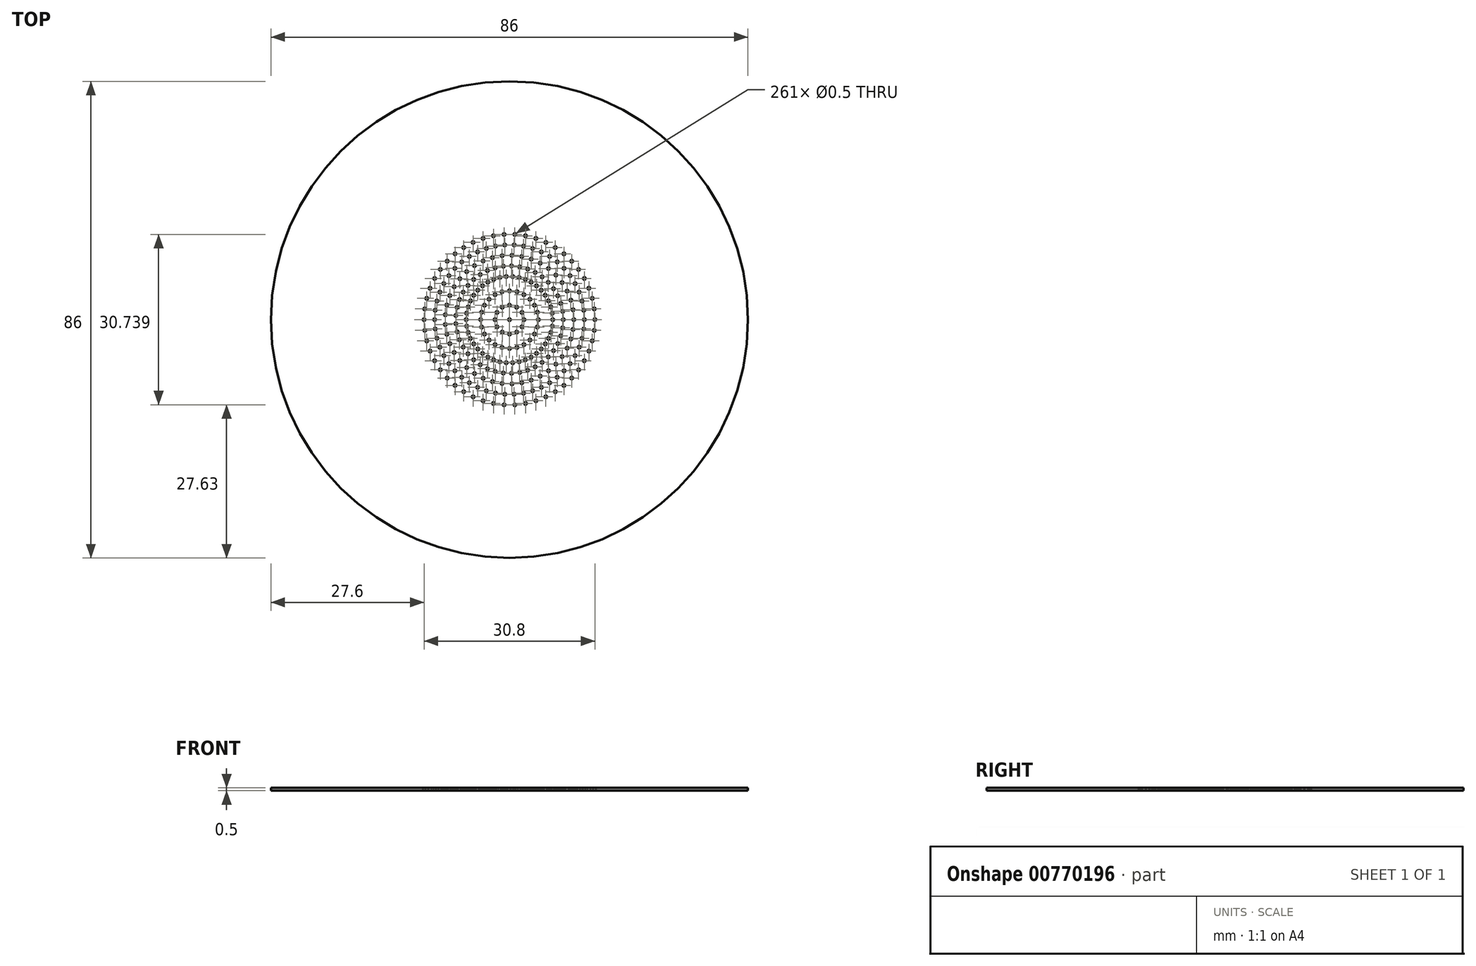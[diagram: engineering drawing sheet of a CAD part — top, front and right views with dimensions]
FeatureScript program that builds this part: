
annotation { "Feature Type Name" : "Feature", "Feature Type Description" : "" }
export const myFeature = defineFeature(function(context is Context, id is Id, definition is map)
    precondition{}
    {
        {
            var Q0;
            Q0=qCreatedBy(makeId("Top.planeOp"),FACE);
            var sketch = newSketch(context, id + "F0", { "sketchPlane" : qUnion([Q0])});
            skCircle(sketch, "E0", {"center": v(0, 0) * mm, "radius": 43 * mm});
            skCircle(sketch, "E1", {"center": v(0, 0) * mm, "radius": 16.13 * mm, "construction": true});
            skCircle(sketch, "E2", {"center": v(0, 0) * mm, "radius": 12.7 * mm, "construction": true});
            skCircle(sketch, "E3", {"center": v(0, 0) * mm, "radius": 8.9 * mm, "construction": true});
            skSolve(sketch);
        }
        {
            var Q0;
            Q0=makeQuery(id+"F0.imprint","IMPRINT",FACE,{"disambiguationData":[TD([[makeQuery(id+"F0.imprint","IMPRINT",EDGE,{"derivedFrom":sQuery(id+"F0.wireOp",EDGE,"E0")}),1.0]])]});
            extrude(context, id + "F1", {"entities" : qUnion([Q0]), "oppositeDirection" : true, "depth" : 0.5 * mm, "offsetDistance" : 25 * mm});
        }
        {
            var Q0;
            Q0=makeQuery(id+"F0.imprint","IMPRINT",FACE,{"disambiguationData":[TD([[makeQuery(id+"F0.imprint","IMPRINT",EDGE,{"derivedFrom":sQuery(id+"F0.wireOp",EDGE,"E0")}),1.0]])]});
            var sketch = newSketch(context, id + "F2", { "sketchPlane" : qUnion([Q0])});
            skCircle(sketch, "E4", {"center": v(0, 0) * mm, "radius": 0.25 * mm});
            skSolve(sketch);
        }
        {
            var Q0;
            Q0=makeQuery(id+"F0.imprint","IMPRINT",FACE,{"disambiguationData":[TD([[makeQuery(id+"F0.imprint","IMPRINT",EDGE,{"derivedFrom":sQuery(id+"F0.wireOp",EDGE,"E0")}),1.0]])]});
            var sketch = newSketch(context, id + "F3", { "sketchPlane" : qUnion([Q0])});
            skCircle(sketch, "E5.0", {"center": v(0, 0) * mm, "radius": 0.25 * mm});
            skCircle(sketch, "E6.1.0.0", {"center": v(2.6, 0) * mm, "radius": 0.25 * mm});
            skCircle(sketch, "E6.2.0.0", {"center": v(5.2, 0) * mm, "radius": 0.25 * mm});
            skCircle(sketch, "E6.3.0.0", {"center": v(7.8, 0) * mm, "radius": 0.25 * mm});
            skLineSegment(sketch, "E6.direction1", {"start": v(0, 0) * mm, "end": v(2.6, 0) * mm, "construction": true});
            skCircle(sketch, "E7.1.0", {"center": v(2.25, 1.3) * mm, "radius": 0.25 * mm});
            skCircle(sketch, "E7.2.0", {"center": v(1.3, 2.25) * mm, "radius": 0.25 * mm});
            skCircle(sketch, "E7.3.0", {"center": v(0, 2.6) * mm, "radius": 0.25 * mm});
            skCircle(sketch, "E7.4.0", {"center": v(-1.3, 2.25) * mm, "radius": 0.25 * mm});
            skCircle(sketch, "E7.5.0", {"center": v(-2.25, 1.3) * mm, "radius": 0.25 * mm});
            skCircle(sketch, "E7.6.0", {"center": v(-2.6, 0) * mm, "radius": 0.25 * mm});
            skCircle(sketch, "E7.7.0", {"center": v(-2.25, -1.3) * mm, "radius": 0.25 * mm});
            skCircle(sketch, "E7.8.0", {"center": v(-1.3, -2.25) * mm, "radius": 0.25 * mm});
            skCircle(sketch, "E7.9.0", {"center": v(0, -2.6) * mm, "radius": 0.25 * mm});
            skCircle(sketch, "E7.10.0", {"center": v(1.3, -2.25) * mm, "radius": 0.25 * mm});
            skCircle(sketch, "E7.11.0", {"center": v(2.25, -1.3) * mm, "radius": 0.25 * mm});
            skCircle(sketch, "E8.1.0", {"center": v(5.02, 1.35) * mm, "radius": 0.25 * mm});
            skCircle(sketch, "E8.2.0", {"center": v(4.5, 2.6) * mm, "radius": 0.25 * mm});
            skCircle(sketch, "E8.3.0", {"center": v(3.68, 3.68) * mm, "radius": 0.25 * mm});
            skCircle(sketch, "E8.4.0", {"center": v(2.6, 4.5) * mm, "radius": 0.25 * mm});
            skCircle(sketch, "E8.5.0", {"center": v(1.35, 5.02) * mm, "radius": 0.25 * mm});
            skCircle(sketch, "E8.6.0", {"center": v(0, 5.2) * mm, "radius": 0.25 * mm});
            skCircle(sketch, "E8.7.0", {"center": v(-1.35, 5.02) * mm, "radius": 0.25 * mm});
            skCircle(sketch, "E8.8.0", {"center": v(-2.6, 4.5) * mm, "radius": 0.25 * mm});
            skCircle(sketch, "E8.9.0", {"center": v(-3.68, 3.68) * mm, "radius": 0.25 * mm});
            skCircle(sketch, "E8.10.0", {"center": v(-4.5, 2.6) * mm, "radius": 0.25 * mm});
            skCircle(sketch, "E8.11.0", {"center": v(-5.02, 1.35) * mm, "radius": 0.25 * mm});
            skCircle(sketch, "E8.12.0", {"center": v(-5.2, 0) * mm, "radius": 0.25 * mm});
            skCircle(sketch, "E8.13.0", {"center": v(-5.02, -1.35) * mm, "radius": 0.25 * mm});
            skCircle(sketch, "E8.14.0", {"center": v(-4.5, -2.6) * mm, "radius": 0.25 * mm});
            skCircle(sketch, "E8.15.0", {"center": v(-3.68, -3.68) * mm, "radius": 0.25 * mm});
            skCircle(sketch, "E8.16.0", {"center": v(-2.6, -4.5) * mm, "radius": 0.25 * mm});
            skCircle(sketch, "E8.17.0", {"center": v(-1.35, -5.02) * mm, "radius": 0.25 * mm});
            skCircle(sketch, "E8.18.0", {"center": v(0, -5.2) * mm, "radius": 0.25 * mm});
            skCircle(sketch, "E8.19.0", {"center": v(1.35, -5.02) * mm, "radius": 0.25 * mm});
            skCircle(sketch, "E8.20.0", {"center": v(2.6, -4.5) * mm, "radius": 0.25 * mm});
            skCircle(sketch, "E8.21.0", {"center": v(3.68, -3.68) * mm, "radius": 0.25 * mm});
            skCircle(sketch, "E8.22.0", {"center": v(4.5, -2.6) * mm, "radius": 0.25 * mm});
            skCircle(sketch, "E8.23.0", {"center": v(5.02, -1.35) * mm, "radius": 0.25 * mm});
            skCircle(sketch, "E9.1.0", {"center": v(7.71, 1.16) * mm, "radius": 0.25 * mm});
            skCircle(sketch, "E9.2.0", {"center": v(7.45, 2.3) * mm, "radius": 0.25 * mm});
            skCircle(sketch, "E9.3.0", {"center": v(7.03, 3.38) * mm, "radius": 0.25 * mm});
            skCircle(sketch, "E9.4.0", {"center": v(6.44, 4.4) * mm, "radius": 0.25 * mm});
            skCircle(sketch, "E9.5.0", {"center": v(5.72, 5.3) * mm, "radius": 0.25 * mm});
            skCircle(sketch, "E9.6.0", {"center": v(4.86, 6.1) * mm, "radius": 0.25 * mm});
            skCircle(sketch, "E9.7.0", {"center": v(3.9, 6.75) * mm, "radius": 0.25 * mm});
            skCircle(sketch, "E9.8.0", {"center": v(2.85, 7.26) * mm, "radius": 0.25 * mm});
            skCircle(sketch, "E9.9.0", {"center": v(1.74, 7.6) * mm, "radius": 0.25 * mm});
            skCircle(sketch, "E9.10.0", {"center": v(0.58, 7.78) * mm, "radius": 0.25 * mm});
            skCircle(sketch, "E9.11.0", {"center": v(-0.58, 7.78) * mm, "radius": 0.25 * mm});
            skCircle(sketch, "E9.12.0", {"center": v(-1.74, 7.6) * mm, "radius": 0.25 * mm});
            skCircle(sketch, "E9.13.0", {"center": v(-2.85, 7.26) * mm, "radius": 0.25 * mm});
            skCircle(sketch, "E9.14.0", {"center": v(-3.9, 6.75) * mm, "radius": 0.25 * mm});
            skCircle(sketch, "E9.15.0", {"center": v(-4.86, 6.1) * mm, "radius": 0.25 * mm});
            skCircle(sketch, "E9.16.0", {"center": v(-5.72, 5.3) * mm, "radius": 0.25 * mm});
            skCircle(sketch, "E9.17.0", {"center": v(-6.44, 4.4) * mm, "radius": 0.25 * mm});
            skCircle(sketch, "E9.18.0", {"center": v(-7.03, 3.38) * mm, "radius": 0.25 * mm});
            skCircle(sketch, "E9.19.0", {"center": v(-7.45, 2.3) * mm, "radius": 0.25 * mm});
            skCircle(sketch, "E9.20.0", {"center": v(-7.71, 1.16) * mm, "radius": 0.25 * mm});
            skCircle(sketch, "E9.21.0", {"center": v(-7.8, 0) * mm, "radius": 0.25 * mm});
            skCircle(sketch, "E9.22.0", {"center": v(-7.71, -1.16) * mm, "radius": 0.25 * mm});
            skCircle(sketch, "E9.23.0", {"center": v(-7.45, -2.3) * mm, "radius": 0.25 * mm});
            skCircle(sketch, "E9.24.0", {"center": v(-7.03, -3.38) * mm, "radius": 0.25 * mm});
            skCircle(sketch, "E9.25.0", {"center": v(-6.44, -4.4) * mm, "radius": 0.25 * mm});
            skCircle(sketch, "E9.26.0", {"center": v(-5.72, -5.3) * mm, "radius": 0.25 * mm});
            skCircle(sketch, "E9.27.0", {"center": v(-4.86, -6.1) * mm, "radius": 0.25 * mm});
            skCircle(sketch, "E9.28.0", {"center": v(-3.9, -6.75) * mm, "radius": 0.25 * mm});
            skCircle(sketch, "E9.29.0", {"center": v(-2.85, -7.26) * mm, "radius": 0.25 * mm});
            skCircle(sketch, "E9.30.0", {"center": v(-1.74, -7.6) * mm, "radius": 0.25 * mm});
            skCircle(sketch, "E9.31.0", {"center": v(-0.58, -7.78) * mm, "radius": 0.25 * mm});
            skCircle(sketch, "E9.32.0", {"center": v(0.58, -7.78) * mm, "radius": 0.25 * mm});
            skCircle(sketch, "E9.33.0", {"center": v(1.74, -7.6) * mm, "radius": 0.25 * mm});
            skCircle(sketch, "E9.34.0", {"center": v(2.85, -7.26) * mm, "radius": 0.25 * mm});
            skCircle(sketch, "E9.35.0", {"center": v(3.9, -6.75) * mm, "radius": 0.25 * mm});
            skCircle(sketch, "E9.36.0", {"center": v(4.86, -6.1) * mm, "radius": 0.25 * mm});
            skCircle(sketch, "E9.37.0", {"center": v(5.72, -5.3) * mm, "radius": 0.25 * mm});
            skCircle(sketch, "E9.38.0", {"center": v(6.44, -4.4) * mm, "radius": 0.25 * mm});
            skCircle(sketch, "E9.39.0", {"center": v(7.03, -3.38) * mm, "radius": 0.25 * mm});
            skCircle(sketch, "E9.40.0", {"center": v(7.45, -2.3) * mm, "radius": 0.25 * mm});
            skCircle(sketch, "E9.41.0", {"center": v(7.71, -1.16) * mm, "radius": 0.25 * mm});
            skSolve(sketch);
        }
        {
            var Q0;
            Q0=makeQuery(id+"F0.imprint","IMPRINT",FACE,{"disambiguationData":[TD([[makeQuery(id+"F0.imprint","IMPRINT",EDGE,{"derivedFrom":sQuery(id+"F0.wireOp",EDGE,"E0")}),1.0]])]});
            var sketch = newSketch(context, id + "F4", { "sketchPlane" : qUnion([Q0])});
            skCircle(sketch, "E10.0", {"center": v(7.8, 0) * mm, "radius": 0.25 * mm});
            skCircle(sketch, "E11.1.0.0", {"center": v(9.7, 0) * mm, "radius": 0.25 * mm});
            skCircle(sketch, "E11.2.0.0", {"center": v(11.6, 0) * mm, "radius": 0.25 * mm});
            skLineSegment(sketch, "E11.direction1", {"start": v(7.8, 0) * mm, "end": v(9.7, 0) * mm, "construction": true});
            skCircle(sketch, "E12.1.0", {"center": v(9.59, 1.48) * mm, "radius": 0.25 * mm});
            skCircle(sketch, "E12.1.1", {"center": v(11.46, 1.77) * mm, "radius": 0.25 * mm});
            skCircle(sketch, "E12.2.0", {"center": v(9.25, 2.93) * mm, "radius": 0.25 * mm});
            skCircle(sketch, "E12.2.1", {"center": v(11.06, 3.5) * mm, "radius": 0.25 * mm});
            skCircle(sketch, "E12.3.0", {"center": v(8.7, 4.3) * mm, "radius": 0.25 * mm});
            skCircle(sketch, "E12.3.1", {"center": v(10.4, 5.15) * mm, "radius": 0.25 * mm});
            skCircle(sketch, "E12.4.0", {"center": v(7.93, 5.58) * mm, "radius": 0.25 * mm});
            skCircle(sketch, "E12.4.1", {"center": v(9.49, 6.67) * mm, "radius": 0.25 * mm});
            skCircle(sketch, "E12.5.0", {"center": v(6.99, 6.73) * mm, "radius": 0.25 * mm});
            skCircle(sketch, "E12.5.1", {"center": v(8.36, 8.04) * mm, "radius": 0.25 * mm});
            skCircle(sketch, "E12.6.0", {"center": v(5.88, 7.71) * mm, "radius": 0.25 * mm});
            skCircle(sketch, "E12.6.1", {"center": v(7.03, 9.23) * mm, "radius": 0.25 * mm});
            skCircle(sketch, "E12.7.0", {"center": v(4.63, 8.52) * mm, "radius": 0.25 * mm});
            skCircle(sketch, "E12.7.1", {"center": v(5.54, 10.2) * mm, "radius": 0.25 * mm});
            skCircle(sketch, "E12.8.0", {"center": v(3.28, 9.13) * mm, "radius": 0.25 * mm});
            skCircle(sketch, "E12.8.1", {"center": v(3.92, 10.92) * mm, "radius": 0.25 * mm});
            skCircle(sketch, "E12.9.0", {"center": v(1.85, 9.52) * mm, "radius": 0.25 * mm});
            skCircle(sketch, "E12.9.1", {"center": v(2.2, 11.39) * mm, "radius": 0.25 * mm});
            skCircle(sketch, "E12.10.0", {"center": v(0.37, 9.7) * mm, "radius": 0.25 * mm});
            skCircle(sketch, "E12.10.1", {"center": v(0.44, 11.6) * mm, "radius": 0.25 * mm});
            skCircle(sketch, "E12.11.0", {"center": v(-1.11, 9.64) * mm, "radius": 0.25 * mm});
            skCircle(sketch, "E12.11.1", {"center": v(-1.33, 11.52) * mm, "radius": 0.25 * mm});
            skCircle(sketch, "E12.12.0", {"center": v(-2.57, 9.35) * mm, "radius": 0.25 * mm});
            skCircle(sketch, "E12.12.1", {"center": v(-3.07, 11.19) * mm, "radius": 0.25 * mm});
            skCircle(sketch, "E12.13.0", {"center": v(-3.97, 8.85) * mm, "radius": 0.25 * mm});
            skCircle(sketch, "E12.13.1", {"center": v(-4.75, 10.59) * mm, "radius": 0.25 * mm});
            skCircle(sketch, "E12.14.0", {"center": v(-5.27, 8.14) * mm, "radius": 0.25 * mm});
            skCircle(sketch, "E12.14.1", {"center": v(-6.3, 9.74) * mm, "radius": 0.25 * mm});
            skCircle(sketch, "E12.15.0", {"center": v(-6.45, 7.24) * mm, "radius": 0.25 * mm});
            skCircle(sketch, "E12.15.1", {"center": v(-7.72, 8.66) * mm, "radius": 0.25 * mm});
            skCircle(sketch, "E12.16.0", {"center": v(-7.48, 6.17) * mm, "radius": 0.25 * mm});
            skCircle(sketch, "E12.16.1", {"center": v(-8.95, 7.38) * mm, "radius": 0.25 * mm});
            skCircle(sketch, "E12.17.0", {"center": v(-8.34, 4.96) * mm, "radius": 0.25 * mm});
            skCircle(sketch, "E12.17.1", {"center": v(-9.97, 5.93) * mm, "radius": 0.25 * mm});
            skCircle(sketch, "E12.18.0", {"center": v(-9, 3.63) * mm, "radius": 0.25 * mm});
            skCircle(sketch, "E12.18.1", {"center": v(-10.76, 4.34) * mm, "radius": 0.25 * mm});
            skCircle(sketch, "E12.19.0", {"center": v(-9.44, 2.21) * mm, "radius": 0.25 * mm});
            skCircle(sketch, "E12.19.1", {"center": v(-11.3, 2.64) * mm, "radius": 0.25 * mm});
            skCircle(sketch, "E12.20.0", {"center": v(-9.67, 0.74) * mm, "radius": 0.25 * mm});
            skCircle(sketch, "E12.20.1", {"center": v(-11.57, 0.89) * mm, "radius": 0.25 * mm});
            skCircle(sketch, "E12.21.0", {"center": v(-9.67, -0.74) * mm, "radius": 0.25 * mm});
            skCircle(sketch, "E12.21.1", {"center": v(-11.57, -0.89) * mm, "radius": 0.25 * mm});
            skCircle(sketch, "E12.22.0", {"center": v(-9.44, -2.21) * mm, "radius": 0.25 * mm});
            skCircle(sketch, "E12.22.1", {"center": v(-11.3, -2.64) * mm, "radius": 0.25 * mm});
            skCircle(sketch, "E12.23.0", {"center": v(-9, -3.63) * mm, "radius": 0.25 * mm});
            skCircle(sketch, "E12.23.1", {"center": v(-10.76, -4.34) * mm, "radius": 0.25 * mm});
            skCircle(sketch, "E12.24.0", {"center": v(-8.34, -4.96) * mm, "radius": 0.25 * mm});
            skCircle(sketch, "E12.24.1", {"center": v(-9.97, -5.93) * mm, "radius": 0.25 * mm});
            skCircle(sketch, "E12.25.0", {"center": v(-7.48, -6.17) * mm, "radius": 0.25 * mm});
            skCircle(sketch, "E12.25.1", {"center": v(-8.95, -7.38) * mm, "radius": 0.25 * mm});
            skCircle(sketch, "E12.26.0", {"center": v(-6.45, -7.24) * mm, "radius": 0.25 * mm});
            skCircle(sketch, "E12.26.1", {"center": v(-7.72, -8.66) * mm, "radius": 0.25 * mm});
            skCircle(sketch, "E12.27.0", {"center": v(-5.27, -8.14) * mm, "radius": 0.25 * mm});
            skCircle(sketch, "E12.27.1", {"center": v(-6.3, -9.74) * mm, "radius": 0.25 * mm});
            skCircle(sketch, "E12.28.0", {"center": v(-3.97, -8.85) * mm, "radius": 0.25 * mm});
            skCircle(sketch, "E12.28.1", {"center": v(-4.75, -10.59) * mm, "radius": 0.25 * mm});
            skCircle(sketch, "E12.29.0", {"center": v(-2.57, -9.35) * mm, "radius": 0.25 * mm});
            skCircle(sketch, "E12.29.1", {"center": v(-3.07, -11.19) * mm, "radius": 0.25 * mm});
            skCircle(sketch, "E12.30.0", {"center": v(-1.11, -9.64) * mm, "radius": 0.25 * mm});
            skCircle(sketch, "E12.30.1", {"center": v(-1.33, -11.52) * mm, "radius": 0.25 * mm});
            skCircle(sketch, "E12.31.0", {"center": v(0.37, -9.7) * mm, "radius": 0.25 * mm});
            skCircle(sketch, "E12.31.1", {"center": v(0.44, -11.6) * mm, "radius": 0.25 * mm});
            skCircle(sketch, "E12.32.0", {"center": v(1.85, -9.52) * mm, "radius": 0.25 * mm});
            skCircle(sketch, "E12.32.1", {"center": v(2.2, -11.39) * mm, "radius": 0.25 * mm});
            skCircle(sketch, "E12.33.0", {"center": v(3.28, -9.13) * mm, "radius": 0.25 * mm});
            skCircle(sketch, "E12.33.1", {"center": v(3.92, -10.92) * mm, "radius": 0.25 * mm});
            skCircle(sketch, "E12.34.0", {"center": v(4.63, -8.52) * mm, "radius": 0.25 * mm});
            skCircle(sketch, "E12.34.1", {"center": v(5.54, -10.2) * mm, "radius": 0.25 * mm});
            skCircle(sketch, "E12.35.0", {"center": v(5.88, -7.71) * mm, "radius": 0.25 * mm});
            skCircle(sketch, "E12.35.1", {"center": v(7.03, -9.23) * mm, "radius": 0.25 * mm});
            skCircle(sketch, "E12.36.0", {"center": v(6.99, -6.73) * mm, "radius": 0.25 * mm});
            skCircle(sketch, "E12.36.1", {"center": v(8.36, -8.04) * mm, "radius": 0.25 * mm});
            skCircle(sketch, "E12.37.0", {"center": v(7.93, -5.58) * mm, "radius": 0.25 * mm});
            skCircle(sketch, "E12.37.1", {"center": v(9.49, -6.67) * mm, "radius": 0.25 * mm});
            skCircle(sketch, "E12.38.0", {"center": v(8.7, -4.3) * mm, "radius": 0.25 * mm});
            skCircle(sketch, "E12.38.1", {"center": v(10.4, -5.15) * mm, "radius": 0.25 * mm});
            skCircle(sketch, "E12.39.0", {"center": v(9.25, -2.93) * mm, "radius": 0.25 * mm});
            skCircle(sketch, "E12.39.1", {"center": v(11.06, -3.5) * mm, "radius": 0.25 * mm});
            skCircle(sketch, "E12.40.0", {"center": v(9.59, -1.48) * mm, "radius": 0.25 * mm});
            skCircle(sketch, "E12.40.1", {"center": v(11.46, -1.77) * mm, "radius": 0.25 * mm});
            skPoint(sketch, "E12.center", {"position": v(0, 0) * mm});
            skSolve(sketch);
        }
        {
            var Q0;
            Q0=makeQuery(id+"F0.imprint","IMPRINT",FACE,{"disambiguationData":[TD([[makeQuery(id+"F0.imprint","IMPRINT",EDGE,{"derivedFrom":sQuery(id+"F0.wireOp",EDGE,"E0")}),1.0]])]});
            var sketch = newSketch(context, id + "F5", { "sketchPlane" : qUnion([Q0])});
            skCircle(sketch, "E13.0", {"center": v(11.6, 0) * mm, "radius": 0.25 * mm});
            skCircle(sketch, "E14.1.0.0", {"center": v(13.5, 0) * mm, "radius": 0.25 * mm});
            skCircle(sketch, "E14.2.0.0", {"center": v(15.4, 0) * mm, "radius": 0.25 * mm});
            skLineSegment(sketch, "E14.direction1", {"start": v(11.6, 0) * mm, "end": v(13.5, 0) * mm, "construction": true});
            skCircle(sketch, "E15.1.0", {"center": v(13.4, 1.7) * mm, "radius": 0.25 * mm});
            skCircle(sketch, "E15.1.1", {"center": v(15.28, 1.93) * mm, "radius": 0.25 * mm});
            skCircle(sketch, "E15.2.0", {"center": v(13.08, 3.36) * mm, "radius": 0.25 * mm});
            skCircle(sketch, "E15.2.1", {"center": v(14.92, 3.83) * mm, "radius": 0.25 * mm});
            skCircle(sketch, "E15.3.0", {"center": v(12.55, 4.97) * mm, "radius": 0.25 * mm});
            skCircle(sketch, "E15.3.1", {"center": v(14.32, 5.67) * mm, "radius": 0.25 * mm});
            skCircle(sketch, "E15.4.0", {"center": v(11.83, 6.5) * mm, "radius": 0.25 * mm});
            skCircle(sketch, "E15.4.1", {"center": v(13.5, 7.42) * mm, "radius": 0.25 * mm});
            skCircle(sketch, "E15.5.0", {"center": v(10.92, 7.94) * mm, "radius": 0.25 * mm});
            skCircle(sketch, "E15.5.1", {"center": v(12.46, 9.05) * mm, "radius": 0.25 * mm});
            skCircle(sketch, "E15.6.0", {"center": v(9.84, 9.24) * mm, "radius": 0.25 * mm});
            skCircle(sketch, "E15.6.1", {"center": v(11.23, 10.54) * mm, "radius": 0.25 * mm});
            skCircle(sketch, "E15.7.0", {"center": v(8.6, 10.4) * mm, "radius": 0.25 * mm});
            skCircle(sketch, "E15.7.1", {"center": v(9.82, 11.87) * mm, "radius": 0.25 * mm});
            skCircle(sketch, "E15.8.0", {"center": v(7.23, 11.4) * mm, "radius": 0.25 * mm});
            skCircle(sketch, "E15.8.1", {"center": v(8.25, 13) * mm, "radius": 0.25 * mm});
            skCircle(sketch, "E15.9.0", {"center": v(5.75, 12.22) * mm, "radius": 0.25 * mm});
            skCircle(sketch, "E15.9.1", {"center": v(6.56, 13.93) * mm, "radius": 0.25 * mm});
            skCircle(sketch, "E15.10.0", {"center": v(4.17, 12.84) * mm, "radius": 0.25 * mm});
            skCircle(sketch, "E15.10.1", {"center": v(4.76, 14.65) * mm, "radius": 0.25 * mm});
            skCircle(sketch, "E15.11.0", {"center": v(2.53, 13.26) * mm, "radius": 0.25 * mm});
            skCircle(sketch, "E15.11.1", {"center": v(2.89, 15.13) * mm, "radius": 0.25 * mm});
            skCircle(sketch, "E15.12.0", {"center": v(0.85, 13.47) * mm, "radius": 0.25 * mm});
            skCircle(sketch, "E15.12.1", {"center": v(0.97, 15.37) * mm, "radius": 0.25 * mm});
            skCircle(sketch, "E15.13.0", {"center": v(-0.85, 13.47) * mm, "radius": 0.25 * mm});
            skCircle(sketch, "E15.13.1", {"center": v(-0.97, 15.37) * mm, "radius": 0.25 * mm});
            skCircle(sketch, "E15.14.0", {"center": v(-2.53, 13.26) * mm, "radius": 0.25 * mm});
            skCircle(sketch, "E15.14.1", {"center": v(-2.89, 15.13) * mm, "radius": 0.25 * mm});
            skCircle(sketch, "E15.15.0", {"center": v(-4.17, 12.84) * mm, "radius": 0.25 * mm});
            skCircle(sketch, "E15.15.1", {"center": v(-4.76, 14.65) * mm, "radius": 0.25 * mm});
            skCircle(sketch, "E15.16.0", {"center": v(-5.75, 12.22) * mm, "radius": 0.25 * mm});
            skCircle(sketch, "E15.16.1", {"center": v(-6.56, 13.93) * mm, "radius": 0.25 * mm});
            skCircle(sketch, "E15.17.0", {"center": v(-7.23, 11.4) * mm, "radius": 0.25 * mm});
            skCircle(sketch, "E15.17.1", {"center": v(-8.25, 13) * mm, "radius": 0.25 * mm});
            skCircle(sketch, "E15.18.0", {"center": v(-8.6, 10.4) * mm, "radius": 0.25 * mm});
            skCircle(sketch, "E15.18.1", {"center": v(-9.82, 11.87) * mm, "radius": 0.25 * mm});
            skCircle(sketch, "E15.19.0", {"center": v(-9.84, 9.24) * mm, "radius": 0.25 * mm});
            skCircle(sketch, "E15.19.1", {"center": v(-11.23, 10.54) * mm, "radius": 0.25 * mm});
            skCircle(sketch, "E15.20.0", {"center": v(-10.92, 7.94) * mm, "radius": 0.25 * mm});
            skCircle(sketch, "E15.20.1", {"center": v(-12.46, 9.05) * mm, "radius": 0.25 * mm});
            skCircle(sketch, "E15.21.0", {"center": v(-11.83, 6.5) * mm, "radius": 0.25 * mm});
            skCircle(sketch, "E15.21.1", {"center": v(-13.5, 7.42) * mm, "radius": 0.25 * mm});
            skCircle(sketch, "E15.22.0", {"center": v(-12.55, 4.97) * mm, "radius": 0.25 * mm});
            skCircle(sketch, "E15.22.1", {"center": v(-14.32, 5.67) * mm, "radius": 0.25 * mm});
            skCircle(sketch, "E15.23.0", {"center": v(-13.08, 3.36) * mm, "radius": 0.25 * mm});
            skCircle(sketch, "E15.23.1", {"center": v(-14.92, 3.83) * mm, "radius": 0.25 * mm});
            skCircle(sketch, "E15.24.0", {"center": v(-13.4, 1.7) * mm, "radius": 0.25 * mm});
            skCircle(sketch, "E15.24.1", {"center": v(-15.28, 1.93) * mm, "radius": 0.25 * mm});
            skCircle(sketch, "E15.25.0", {"center": v(-13.5, 0) * mm, "radius": 0.25 * mm});
            skCircle(sketch, "E15.25.1", {"center": v(-15.4, 0) * mm, "radius": 0.25 * mm});
            skCircle(sketch, "E15.26.0", {"center": v(-13.4, -1.7) * mm, "radius": 0.25 * mm});
            skCircle(sketch, "E15.26.1", {"center": v(-15.28, -1.93) * mm, "radius": 0.25 * mm});
            skCircle(sketch, "E15.27.0", {"center": v(-13.08, -3.36) * mm, "radius": 0.25 * mm});
            skCircle(sketch, "E15.27.1", {"center": v(-14.92, -3.83) * mm, "radius": 0.25 * mm});
            skCircle(sketch, "E15.28.0", {"center": v(-12.55, -4.97) * mm, "radius": 0.25 * mm});
            skCircle(sketch, "E15.28.1", {"center": v(-14.32, -5.67) * mm, "radius": 0.25 * mm});
            skCircle(sketch, "E15.29.0", {"center": v(-11.83, -6.5) * mm, "radius": 0.25 * mm});
            skCircle(sketch, "E15.29.1", {"center": v(-13.5, -7.42) * mm, "radius": 0.25 * mm});
            skCircle(sketch, "E15.30.0", {"center": v(-10.92, -7.94) * mm, "radius": 0.25 * mm});
            skCircle(sketch, "E15.30.1", {"center": v(-12.46, -9.05) * mm, "radius": 0.25 * mm});
            skCircle(sketch, "E15.31.0", {"center": v(-9.84, -9.24) * mm, "radius": 0.25 * mm});
            skCircle(sketch, "E15.31.1", {"center": v(-11.23, -10.54) * mm, "radius": 0.25 * mm});
            skCircle(sketch, "E15.32.0", {"center": v(-8.6, -10.4) * mm, "radius": 0.25 * mm});
            skCircle(sketch, "E15.32.1", {"center": v(-9.82, -11.87) * mm, "radius": 0.25 * mm});
            skCircle(sketch, "E15.33.0", {"center": v(-7.23, -11.4) * mm, "radius": 0.25 * mm});
            skCircle(sketch, "E15.33.1", {"center": v(-8.25, -13) * mm, "radius": 0.25 * mm});
            skCircle(sketch, "E15.34.0", {"center": v(-5.75, -12.22) * mm, "radius": 0.25 * mm});
            skCircle(sketch, "E15.34.1", {"center": v(-6.56, -13.93) * mm, "radius": 0.25 * mm});
            skCircle(sketch, "E15.35.0", {"center": v(-4.17, -12.84) * mm, "radius": 0.25 * mm});
            skCircle(sketch, "E15.35.1", {"center": v(-4.76, -14.65) * mm, "radius": 0.25 * mm});
            skCircle(sketch, "E15.36.0", {"center": v(-2.53, -13.26) * mm, "radius": 0.25 * mm});
            skCircle(sketch, "E15.36.1", {"center": v(-2.89, -15.13) * mm, "radius": 0.25 * mm});
            skCircle(sketch, "E15.37.0", {"center": v(-0.85, -13.47) * mm, "radius": 0.25 * mm});
            skCircle(sketch, "E15.37.1", {"center": v(-0.97, -15.37) * mm, "radius": 0.25 * mm});
            skCircle(sketch, "E15.38.0", {"center": v(0.85, -13.47) * mm, "radius": 0.25 * mm});
            skCircle(sketch, "E15.38.1", {"center": v(0.97, -15.37) * mm, "radius": 0.25 * mm});
            skCircle(sketch, "E15.39.0", {"center": v(2.53, -13.26) * mm, "radius": 0.25 * mm});
            skCircle(sketch, "E15.39.1", {"center": v(2.89, -15.13) * mm, "radius": 0.25 * mm});
            skCircle(sketch, "E15.40.0", {"center": v(4.17, -12.84) * mm, "radius": 0.25 * mm});
            skCircle(sketch, "E15.40.1", {"center": v(4.76, -14.65) * mm, "radius": 0.25 * mm});
            skCircle(sketch, "E15.41.0", {"center": v(5.75, -12.22) * mm, "radius": 0.25 * mm});
            skCircle(sketch, "E15.41.1", {"center": v(6.56, -13.93) * mm, "radius": 0.25 * mm});
            skCircle(sketch, "E15.42.0", {"center": v(7.23, -11.4) * mm, "radius": 0.25 * mm});
            skCircle(sketch, "E15.42.1", {"center": v(8.25, -13) * mm, "radius": 0.25 * mm});
            skCircle(sketch, "E15.43.0", {"center": v(8.6, -10.4) * mm, "radius": 0.25 * mm});
            skCircle(sketch, "E15.43.1", {"center": v(9.82, -11.87) * mm, "radius": 0.25 * mm});
            skCircle(sketch, "E15.44.0", {"center": v(9.84, -9.24) * mm, "radius": 0.25 * mm});
            skCircle(sketch, "E15.44.1", {"center": v(11.23, -10.54) * mm, "radius": 0.25 * mm});
            skCircle(sketch, "E15.45.0", {"center": v(10.92, -7.94) * mm, "radius": 0.25 * mm});
            skCircle(sketch, "E15.45.1", {"center": v(12.46, -9.05) * mm, "radius": 0.25 * mm});
            skCircle(sketch, "E15.46.0", {"center": v(11.83, -6.5) * mm, "radius": 0.25 * mm});
            skCircle(sketch, "E15.46.1", {"center": v(13.5, -7.42) * mm, "radius": 0.25 * mm});
            skCircle(sketch, "E15.47.0", {"center": v(12.55, -4.97) * mm, "radius": 0.25 * mm});
            skCircle(sketch, "E15.47.1", {"center": v(14.32, -5.67) * mm, "radius": 0.25 * mm});
            skCircle(sketch, "E15.48.0", {"center": v(13.08, -3.36) * mm, "radius": 0.25 * mm});
            skCircle(sketch, "E15.48.1", {"center": v(14.92, -3.83) * mm, "radius": 0.25 * mm});
            skCircle(sketch, "E15.49.0", {"center": v(13.4, -1.7) * mm, "radius": 0.25 * mm});
            skCircle(sketch, "E15.49.1", {"center": v(15.28, -1.93) * mm, "radius": 0.25 * mm});
            skPoint(sketch, "E15.center", {"position": v(0, 0) * mm});
            skSolve(sketch);
        }
        {
            var Q0;
            Q0 = qSketchRegion(id + "F2", true);
            var Q1;
            Q1 = qSketchRegion(id + "F3", true);
            var Q2;
            Q2 = qSketchRegion(id + "F4", true);
            var Q3;
            Q3 = qSketchRegion(id + "F5", true);
            extrude(context, id + "F6", {"entities" : qUnion([Q0, Q1, Q2, Q3]), "operationType" : NewBodyOperationType.REMOVE, "oppositeDirection" : true, "depth" : 25 * mm, "offsetDistance" : 25 * mm});
        }
    });
